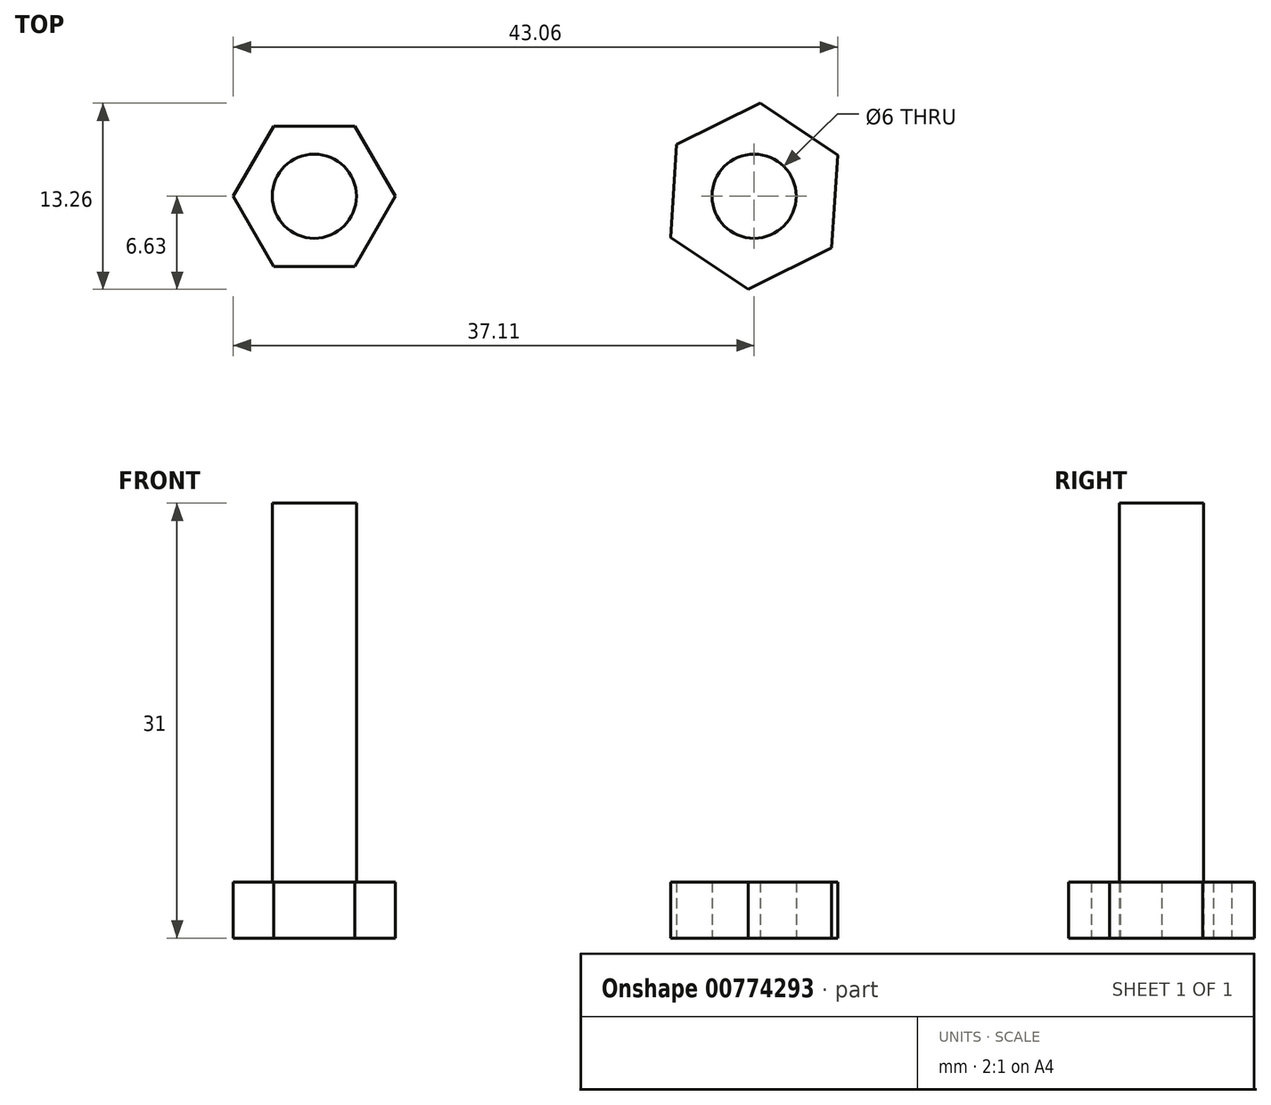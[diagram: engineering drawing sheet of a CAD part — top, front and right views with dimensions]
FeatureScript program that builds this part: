
annotation { "Feature Type Name" : "Feature", "Feature Type Description" : "" }
export const myFeature = defineFeature(function(context is Context, id is Id, definition is map)
    precondition{}
    {
        {
            var Q0;
            Q0=qCreatedBy(makeId("Top.planeOp"),FACE);
            var sketch = newSketch(context, id + "F0", { "sketchPlane" : qUnion([Q0])});
            skLineSegment(sketch, "E0.0", {"start": v(-2.89, 5) * mm, "end": v(2.89, 5) * mm});
            skLineSegment(sketch, "E0.1", {"start": v(2.89, 5) * mm, "end": v(5.77, 0) * mm});
            skLineSegment(sketch, "E0.2", {"start": v(5.77, 0) * mm, "end": v(2.89, -5) * mm});
            skLineSegment(sketch, "E0.3", {"start": v(2.89, -5) * mm, "end": v(-2.89, -5) * mm});
            skLineSegment(sketch, "E0.4", {"start": v(-2.89, -5) * mm, "end": v(-5.77, 0) * mm});
            skLineSegment(sketch, "E0.5", {"start": v(-5.77, 0) * mm, "end": v(-2.89, 5) * mm});
            skCircle(sketch, "E1", {"center": v(0, 0) * mm, "radius": 3 * mm});
            skLineSegment(sketch, "E2", {"start": v(15.67, 9.98) * mm, "end": v(15.67, -17.37) * mm});
            skCircle(sketch, "E3.MirrorC", {"center": v(31.34, 0) * mm, "radius": 3 * mm});
            skLineSegment(sketch, "E4.0", {"start": v(31.77, 6.63) * mm, "end": v(37.3, 2.94) * mm});
            skLineSegment(sketch, "E4.1", {"start": v(37.3, 2.94) * mm, "end": v(36.86, -3.69) * mm});
            skLineSegment(sketch, "E4.2", {"start": v(36.86, -3.69) * mm, "end": v(30.9, -6.63) * mm});
            skLineSegment(sketch, "E4.3", {"start": v(30.9, -6.63) * mm, "end": v(25.39, -2.94) * mm});
            skLineSegment(sketch, "E4.4", {"start": v(25.39, -2.94) * mm, "end": v(25.82, 3.69) * mm});
            skLineSegment(sketch, "E4.5", {"start": v(25.82, 3.69) * mm, "end": v(31.77, 6.63) * mm});
            skSolve(sketch);
        }
        {
            var Q0;
            Q0=makeQuery(id+"F0.imprint","IMPRINT",FACE,{"disambiguationData":[TD([[makeQuery(id+"F0.imprint","IMPRINT",EDGE,{"derivedFrom":sQuery(id+"F0.wireOp",EDGE,"E1")}),1.0]])]});
            extrude(context, id + "F1", {"entities" : qUnion([Q0]), "depth" : 31 * mm, "offsetDistance" : 25 * mm});
        }
        {
            var Q0;
            Q0=makeQuery(id+"F0.imprint","IMPRINT",FACE,{"disambiguationData":[TD([[makeQuery(id+"F0.imprint","IMPRINT",EDGE,{"derivedFrom":sQuery(id+"F0.wireOp",EDGE,"E0.0")}),-1.0]])]});
            extrude(context, id + "F2", {"entities" : qUnion([Q0]), "operationType" : NewBodyOperationType.ADD, "depth" : 4 * mm, "offsetDistance" : 25 * mm});
        }
        {
            var Q0;
            Q0 = qSketchRegion(id + "F0", true);
            extrude(context, id + "F3", {"entities" : qUnion([Q0]), "operationType" : NewBodyOperationType.ADD, "depth" : 4 * mm, "offsetDistance" : 25 * mm});
        }
    });
